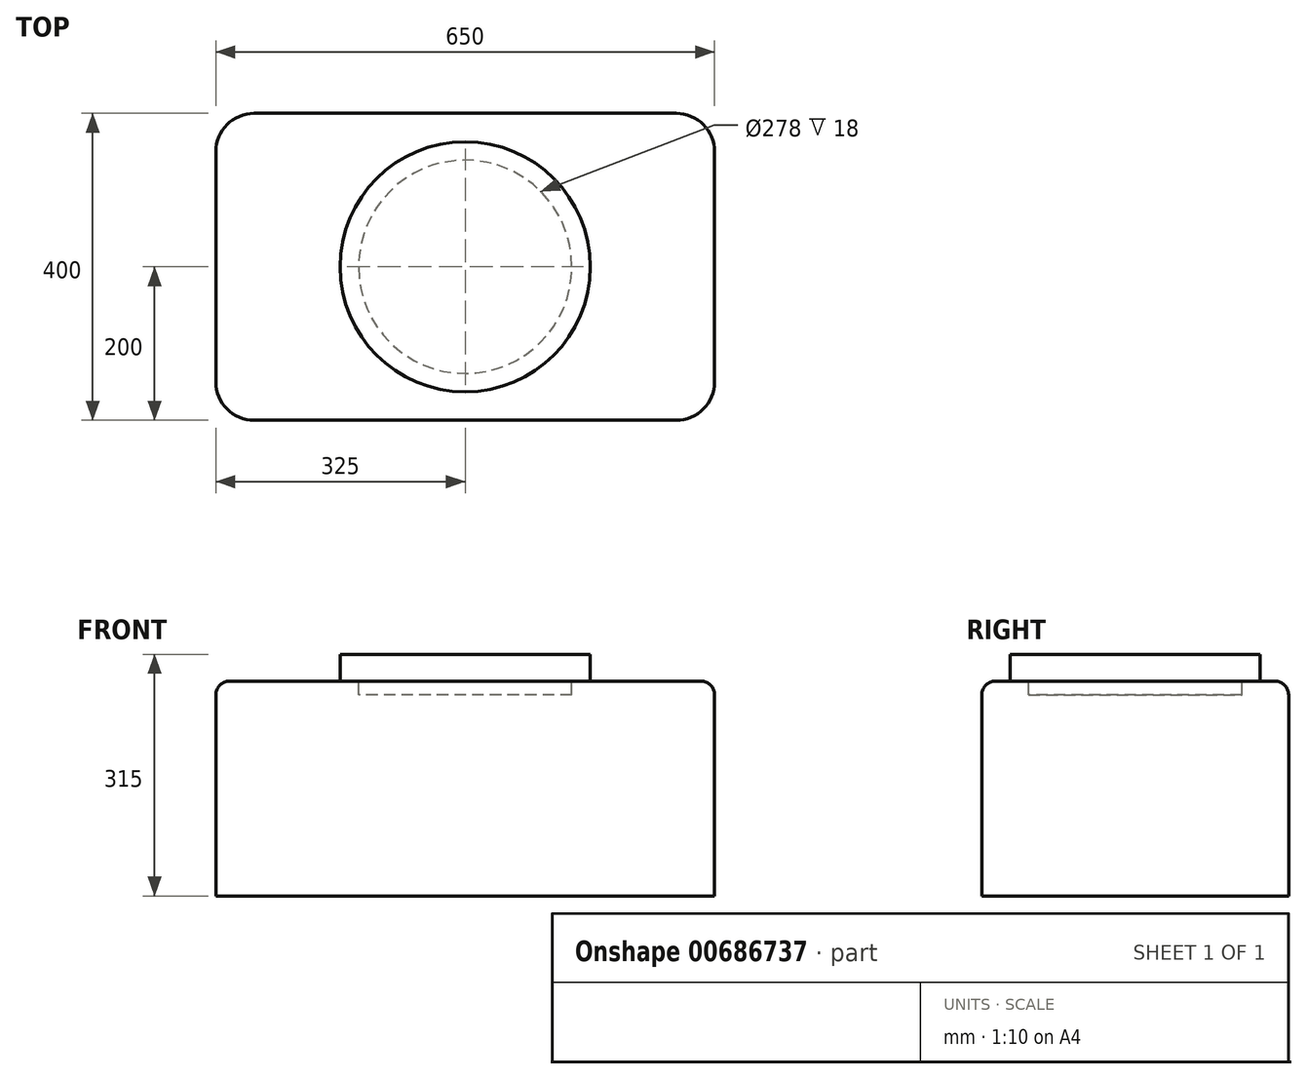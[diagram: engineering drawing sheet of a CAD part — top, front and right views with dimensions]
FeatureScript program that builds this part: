
annotation { "Feature Type Name" : "Feature", "Feature Type Description" : "" }
export const myFeature = defineFeature(function(context is Context, id is Id, definition is map)
    precondition{}
    {
        {
            var Q0;
            Q0=qCreatedBy(makeId("Top.planeOp"),FACE);
            var sketch = newSketch(context, id + "F0", { "sketchPlane" : qUnion([Q0])});
            skLineSegment(sketch, "E0.bottom", {"start": v(325, -200) * mm, "end": v(-325, -200) * mm});
            skLineSegment(sketch, "E0.top", {"start": v(325, 200) * mm, "end": v(-325, 200) * mm});
            skLineSegment(sketch, "E0.left", {"start": v(325, -200) * mm, "end": v(325, 200) * mm});
            skLineSegment(sketch, "E0.right", {"start": v(-325, -200) * mm, "end": v(-325, 200) * mm});
            skPoint(sketch, "E0.middle", {"position": v(0, 0) * mm});
            skSolve(sketch);
        }
        {
            var Q0;
            Q0=makeQuery(id+"F0.imprint","IMPRINT",FACE,{"disambiguationData":[TD([[makeQuery(id+"F0.imprint","IMPRINT",EDGE,{"derivedFrom":sQuery(id+"F0.wireOp",EDGE,"E0.bottom")}),-1.0]])]});
            extrude(context, id + "F1", {"entities" : qUnion([Q0]), "depth" : 280 * mm, "offsetDistance" : 25 * mm});
        }
        {
            var Q0;
            Q0=makeQuery(id+"F1.opExtrude","SWEPT_EDGE",EDGE,{"disambiguationData":[OSD([sQuery(id+"F0.wireOp",EDGE,"E0.bottom"),sQuery(id+"F0.wireOp",EDGE,"E0.left")])]});
            var Q1;
            Q1=makeQuery(id+"F1.opExtrude","SWEPT_EDGE",EDGE,{"disambiguationData":[OSD([sQuery(id+"F0.wireOp",EDGE,"E0.bottom"),sQuery(id+"F0.wireOp",EDGE,"E0.right")])]});
            var Q2;
            Q2=makeQuery(id+"F1.opExtrude","SWEPT_EDGE",EDGE,{"disambiguationData":[OSD([sQuery(id+"F0.wireOp",EDGE,"E0.top"),sQuery(id+"F0.wireOp",EDGE,"E0.left")])]});
            var Q3;
            Q3=makeQuery(id+"F1.opExtrude","SWEPT_EDGE",EDGE,{"disambiguationData":[OSD([sQuery(id+"F0.wireOp",EDGE,"E0.top"),sQuery(id+"F0.wireOp",EDGE,"E0.right")])]});
            fillet(context, id + "F2", {"entities" : qUnion([Q0, Q1, Q2, Q3]), "radius" : 50 * mm, "tangentPropagation" : true, "allowEdgeOverflow" : false});
        }
        {
            var Q0;
            Q0=makeQuery(id+"F1.opExtrude","CAP_FACE",FACE,{"disambiguationData":[OSD([sQuery(id+"F0.wireOp",EDGE,"E0.bottom"),sQuery(id+"F0.wireOp",EDGE,"E0.top"),sQuery(id+"F0.wireOp",EDGE,"E0.left"),sQuery(id+"F0.wireOp",EDGE,"E0.right")])],"isStart":false});
            var sketch = newSketch(context, id + "F3", { "sketchPlane" : qUnion([Q0])});
            skLineSegment(sketch, "E1", {"start": v(0, -200) * mm, "end": v(0, 200) * mm, "construction": true});
            skLineSegment(sketch, "E2", {"start": v(-325, 0) * mm, "end": v(325, 0) * mm, "construction": true});
            skCircle(sketch, "E3", {"center": v(0, 0) * mm, "radius": 139 * mm});
            skSolve(sketch);
        }
        {
            var Q0;
            Q0 = qSketchRegion(id + "F3", true);
            extrude(context, id + "F4", {"entities" : qUnion([Q0]), "operationType" : NewBodyOperationType.REMOVE, "oppositeDirection" : true, "depth" : 18 * mm, "offsetDistance" : 25 * mm});
        }
        {
            var Q0;
            Q0=makeQuery(id+"F1.opExtrude","CAP_FACE",FACE,{"disambiguationData":[OSD([sQuery(id+"F0.wireOp",EDGE,"E0.bottom"),sQuery(id+"F0.wireOp",EDGE,"E0.top"),sQuery(id+"F0.wireOp",EDGE,"E0.left"),sQuery(id+"F0.wireOp",EDGE,"E0.right")])],"isStart":false});
            var sketch = newSketch(context, id + "F5", { "sketchPlane" : qUnion([Q0])});
            skCircle(sketch, "E4", {"center": v(0, 0) * mm, "radius": 163 * mm});
            skSolve(sketch);
        }
        {
            var Q0;
            Q0 = qSketchRegion(id + "F5", true);
            extrude(context, id + "F6", {"entities" : qUnion([Q0]), "depth" : 35 * mm, "offsetDistance" : 25 * mm});
        }
        {
            var Q0;
            Q0=makeQuery(id+"F1.opExtrude","CAP_EDGE",EDGE,{"disambiguationData":[OSD([sQuery(id+"F0.wireOp",EDGE,"E0.bottom")])],"isStart":false});
            fillet(context, id + "F7", {"entities" : qUnion([Q0]), "radius" : 18 * mm, "tangentPropagation" : true, "allowEdgeOverflow" : false});
        }
    });
